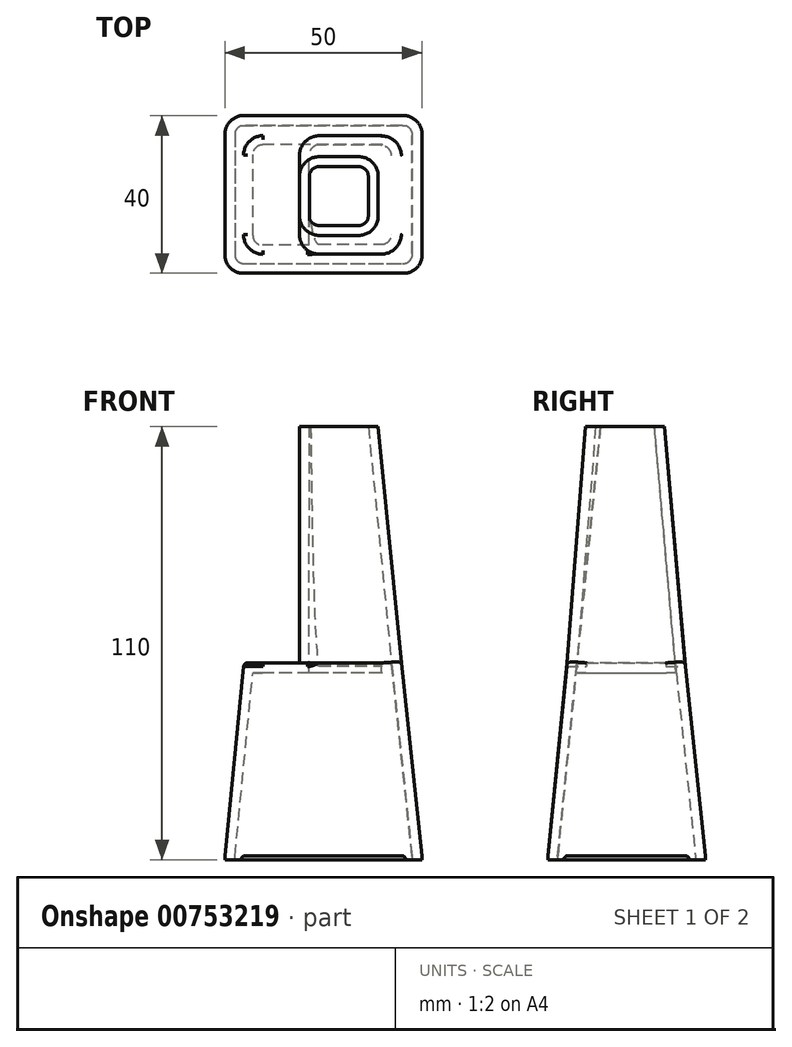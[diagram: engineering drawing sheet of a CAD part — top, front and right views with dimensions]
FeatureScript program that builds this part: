
annotation { "Feature Type Name" : "Feature", "Feature Type Description" : "" }
export const myFeature = defineFeature(function(context is Context, id is Id, definition is map)
    precondition{}
    {
        {
            var Q0;
            Q0=qCreatedBy(makeId("Top.planeOp"),FACE);
            var sketch = newSketch(context, id + "F0", { "sketchPlane" : qUnion([Q0])});
            skLineSegment(sketch, "E0.bottom", {"start": v(-25.66, 21.58) * mm, "end": v(24.34, 21.58) * mm});
            skLineSegment(sketch, "E0.top", {"start": v(-25.66, -18.42) * mm, "end": v(24.34, -18.42) * mm});
            skLineSegment(sketch, "E0.left", {"start": v(-25.66, 21.58) * mm, "end": v(-25.66, -18.42) * mm});
            skLineSegment(sketch, "E0.right", {"start": v(24.34, 21.58) * mm, "end": v(24.34, -18.42) * mm});
            skSolve(sketch);
        }
        {
            var Q0;
            Q0=qCreatedBy(makeId("Top.planeOp"),FACE);
            var Q1;
            Q1 = qBodyType(qCreatedBy(id + "FtEjOQUEwYb0ZHO_0" ,EDGE), BodyType.WIRE);
            cPlane(context, id + "F1", {"entities" : qUnion([Q0, Q1]), "cplaneType" : CPlaneType.OFFSET, "offset" : 50 * mm, "width" : 150 * mm, "height" : 150 * mm});
        }
        {
            var Q0;
            Q0=qCreatedBy(id+"F1.planeOp",FACE);
            var sketch = newSketch(context, id + "F2", { "sketchPlane" : qUnion([Q0])});
            skLineSegment(sketch, "E1.bottom", {"start": v(-20.88, 16.46) * mm, "end": v(19.12, 16.46) * mm});
            skLineSegment(sketch, "E1.top", {"start": v(-20.88, -13.54) * mm, "end": v(19.12, -13.54) * mm});
            skLineSegment(sketch, "E1.left", {"start": v(-20.88, 16.46) * mm, "end": v(-20.88, -13.54) * mm});
            skLineSegment(sketch, "E1.right", {"start": v(19.12, 16.46) * mm, "end": v(19.12, -13.54) * mm});
            skSolve(sketch);
        }
        {
            var Q0;
            Q0 = qSketchRegion(id + "F0", true);
            extrude(context, id + "F3", {"entities" : qUnion([Q0]), "depth" : 1 * mm, "offsetDistance" : 25 * mm});
        }
        {
            var Q0;
            Q0=makeQuery(id+"F3.opExtrude","CAP_FACE",FACE,{"disambiguationData":[OSD([sQuery(id+"F0.wireOp",EDGE,"E0.bottom"),sQuery(id+"F0.wireOp",EDGE,"E0.top"),sQuery(id+"F0.wireOp",EDGE,"E0.left"),sQuery(id+"F0.wireOp",EDGE,"E0.right")])],"isStart":false});
            var Q1;
            Q1=makeQuery(id+"F2.imprint","IMPRINT",FACE,{"disambiguationData":[TD([[makeQuery(id+"F2.imprint","IMPRINT",EDGE,{"derivedFrom":sQuery(id+"F2.wireOp",EDGE,"E1.bottom")}),-1.0]])]});
            loft(context, id + "F4", {"operationType" : NewBodyOperationType.ADD, "sheetProfilesArray" : [{ "sheetProfileEntities" : qUnion([Q0]) }, { "sheetProfileEntities" : qUnion([Q1]) }]});
        }
        {
            var Q0;
            Q0=makeQuery(id+"F4.opLoft","CAP_FACE",FACE,{"disambiguationData":[OSD([makeQuery(id+"F2.imprint","IMPRINT",FACE,{"disambiguationData":[TD([[makeQuery(id+"F2.imprint","IMPRINT",EDGE,{"derivedFrom":sQuery(id+"F2.wireOp",EDGE,"E1.bottom")}),-1.0]])]})])],"isStart":true});
            var sketch = newSketch(context, id + "F5", { "sketchPlane" : qUnion([Q0])});
            skLineSegment(sketch, "E2.bottom", {"start": v(-6.8, -13.54) * mm, "end": v(19.12, -13.54) * mm});
            skLineSegment(sketch, "E2.top", {"start": v(-6.8, 16.46) * mm, "end": v(19.12, 16.46) * mm});
            skLineSegment(sketch, "E2.left", {"start": v(-6.8, -13.54) * mm, "end": v(-6.8, 16.46) * mm});
            skLineSegment(sketch, "E2.right", {"start": v(19.12, -13.54) * mm, "end": v(19.12, 16.46) * mm});
            skSolve(sketch);
        }
        {
            var Q0;
            Q0=qCreatedBy(id+"F1.planeOp",FACE);
            cPlane(context, id + "F6", {"entities" : qUnion([Q0]), "cplaneType" : CPlaneType.OFFSET, "offset" : 60 * mm, "width" : 150 * mm, "height" : 150 * mm});
        }
        {
            var Q0;
            Q0=qCreatedBy(id+"F6.planeOp",FACE);
            var sketch = newSketch(context, id + "F7", { "sketchPlane" : qUnion([Q0])});
            skLineSegment(sketch, "E3.bottom", {"start": v(-6.75, 11.2) * mm, "end": v(13.25, 11.2) * mm});
            skLineSegment(sketch, "E3.top", {"start": v(-6.75, -8.8) * mm, "end": v(13.25, -8.8) * mm});
            skLineSegment(sketch, "E3.left", {"start": v(-6.75, 11.2) * mm, "end": v(-6.75, -8.8) * mm});
            skLineSegment(sketch, "E3.right", {"start": v(13.25, 11.2) * mm, "end": v(13.25, -8.8) * mm});
            skSolve(sketch);
        }
        {
            var Q0;
            Q0=makeQuery(id+"F5.imprint","IMPRINT",FACE,{"disambiguationData":[TD([[makeQuery(id+"F5.imprint","IMPRINT",EDGE,{"derivedFrom":sQuery(id+"F5.wireOp",EDGE,"E2.bottom")}),1.0]])]});
            var Q1;
            Q1=makeQuery(id+"F7.imprint","IMPRINT",FACE,{"disambiguationData":[TD([[makeQuery(id+"F7.imprint","IMPRINT",EDGE,{"derivedFrom":sQuery(id+"F7.wireOp",EDGE,"E3.bottom")}),-1.0]])]});
            loft(context, id + "F8", {"operationType" : NewBodyOperationType.ADD, "sheetProfilesArray" : [{ "sheetProfileEntities" : qUnion([Q0]) }, { "sheetProfileEntities" : qUnion([Q1]) }]});
        }
        {
            var Q0;
            Q0=makeQuery(id+"F4.opLoft","SWEPT_EDGE",EDGE,{"disambiguationData":[OSD([sQuery(id+"F0.wireOp",EDGE,"E0.top"),sQuery(id+"F0.wireOp",EDGE,"E0.right"),sQuery(id+"F2.wireOp",EDGE,"E1.top"),sQuery(id+"F2.wireOp",EDGE,"E1.right")])]});
            var Q1;
            Q1=makeQuery(id+"F8.opLoft","SWEPT_EDGE",EDGE,{"disambiguationData":[OSD([sQuery(id+"F5.wireOp",EDGE,"E2.bottom"),sQuery(id+"F5.wireOp",EDGE,"E2.right"),sQuery(id+"F7.wireOp",EDGE,"E3.top"),sQuery(id+"F7.wireOp",EDGE,"E3.right")])]});
            var Q2;
            Q2=makeQuery(id+"F4.opLoft","SWEPT_EDGE",EDGE,{"disambiguationData":[OSD([sQuery(id+"F0.wireOp",EDGE,"E0.bottom"),sQuery(id+"F0.wireOp",EDGE,"E0.right"),sQuery(id+"F2.wireOp",EDGE,"E1.bottom"),sQuery(id+"F2.wireOp",EDGE,"E1.right")])]});
            var Q3;
            Q3=makeQuery(id+"F8.opLoft","SWEPT_EDGE",EDGE,{"disambiguationData":[OSD([sQuery(id+"F5.wireOp",EDGE,"E2.top"),sQuery(id+"F5.wireOp",EDGE,"E2.right"),sQuery(id+"F7.wireOp",EDGE,"E3.bottom"),sQuery(id+"F7.wireOp",EDGE,"E3.right")])]});
            var Q4;
            Q4=makeQuery(id+"F4.opLoft","SWEPT_EDGE",EDGE,{"disambiguationData":[OSD([sQuery(id+"F0.wireOp",EDGE,"E0.bottom"),sQuery(id+"F0.wireOp",EDGE,"E0.left"),sQuery(id+"F2.wireOp",EDGE,"E1.bottom"),sQuery(id+"F2.wireOp",EDGE,"E1.left")])]});
            var Q5;
            Q5=makeQuery(id+"F4.opLoft","SWEPT_EDGE",EDGE,{"disambiguationData":[OSD([sQuery(id+"F0.wireOp",EDGE,"E0.top"),sQuery(id+"F0.wireOp",EDGE,"E0.left"),sQuery(id+"F2.wireOp",EDGE,"E1.top"),sQuery(id+"F2.wireOp",EDGE,"E1.left")])]});
            var Q6;
            Q6=makeQuery(id+"F8.opLoft","SWEPT_EDGE",EDGE,{"disambiguationData":[OSD([sQuery(id+"F2.wireOp",EDGE,"E1.top"),sQuery(id+"F2.wireOp",EDGE,"E1.left"),sQuery(id+"F2.wireOp",EDGE,"E1.right"),sQuery(id+"F5.wireOp",EDGE,"E2.bottom"),sQuery(id+"F5.wireOp",EDGE,"E2.left"),sQuery(id+"F7.wireOp",EDGE,"E3.top"),sQuery(id+"F7.wireOp",EDGE,"E3.left")])]});
            var Q7;
            Q7=makeQuery(id+"F8.opLoft","SWEPT_EDGE",EDGE,{"disambiguationData":[OSD([sQuery(id+"F2.wireOp",EDGE,"E1.bottom"),sQuery(id+"F2.wireOp",EDGE,"E1.left"),sQuery(id+"F2.wireOp",EDGE,"E1.right"),sQuery(id+"F5.wireOp",EDGE,"E2.top"),sQuery(id+"F5.wireOp",EDGE,"E2.left"),sQuery(id+"F7.wireOp",EDGE,"E3.bottom"),sQuery(id+"F7.wireOp",EDGE,"E3.left")])]});
            fillet(context, id + "F9", {"entities" : qUnion([Q0, Q1, Q2, Q3, Q4, Q5, Q6, Q7]), "tangentPropagation" : true, "radius" : 5 * mm, "defaultsChanged" : false, "vertexSettings" : [], "allowEdgeOverflow" : false});
        }
        {
            var Q0;
            Q0=makeQuery(id+"F8.boolean.opBoolean","SPLIT",EDGE,{"derivedFrom":makeQuery(id+"F4.opLoft","MID_CAP_EDGE",EDGE,{"disambiguationData":[OSD([sQuery(id+"F2.wireOp",EDGE,"E1.bottom"),sQuery(id+"F2.wireOp",EDGE,"E1.left"),sQuery(id+"F2.wireOp",EDGE,"E1.right")])],"capPos":1.0})});
            fillet(context, id + "F10", {"entities" : qUnion([Q0]), "tangentPropagation" : true, "radius" : 1 * mm, "defaultsChanged" : true, "vertexSettings" : [], "allowEdgeOverflow" : false});
        }
        {
            var Q0;
            Q0=makeQuery(id+"F8.opLoft","CAP_FACE",FACE,{"disambiguationData":[OSD([makeQuery(id+"F7.imprint","IMPRINT",FACE,{"disambiguationData":[TD([[makeQuery(id+"F7.imprint","IMPRINT",EDGE,{"derivedFrom":sQuery(id+"F7.wireOp",EDGE,"E3.bottom")}),-1.0]])]})])],"isStart":true});
            var Q1;
            Q1=makeQuery(id+"F3.opExtrude","CAP_FACE",FACE,{"disambiguationData":[OSD([sQuery(id+"F0.wireOp",EDGE,"E0.bottom"),sQuery(id+"F0.wireOp",EDGE,"E0.top"),sQuery(id+"F0.wireOp",EDGE,"E0.left"),sQuery(id+"F0.wireOp",EDGE,"E0.right")])],"isStart":true});
            shell(context, id + "F11", {"entities" : qUnion([Q0, Q1]), "thickness" : 2.5 * mm});
        }
    });
